# Revit family: Plumbing_Drainage_hansgrohe_56188XXX-RainDrain-Allround-Complete-set___555
name_source: partatom
category: Plumbing Fixtures
revit_build: Autodesk Revit 2018 (Build: 20170223_1515(x64)
units: mm (PartAtom-declared; Revit-internal decimal feet)

## family parameters
Cut with Voids When Loaded = Yes
Host = Face
OmniClass Number = 23.31.17.29
OmniClass Title = Shower Drains
Part Type = Normal
Room Calculation Point = No
Round Connector Dimension = Use Diameter
Shared = No

## types (2) — shared parameters
Always visible = Yes
BIMobject category = Drainage
Description = RainDrain Allround Complete set shower drain 900 for standard/flat installation
Design country = Germany
Edition number = 1
IFC Classification = Pipe Fitting
Manufacturer = Hansgrohe
Manufacturer country = Germany
Manufacturer name = hansgrohe
Masterformat 2014 Code = 22 13 19.13
Masterformat 2014 Description = Sanitary Drains
Material 1 = Hansgrohe - Plastic - Gray
Material 2 = Hansgrohe - Metal - 800 Stainless Steel Optic
Model = 56188XXX
OmniClass Code = 23-31 17 29
OmniClass Description = Shower Drains
Product Guid = f0647fe0-2ab4-4b4f-babe-186e32a229ca
Product SKU = 56188XXX
Product data url = https://bimobject.com
Product family = uBox universal
Product group = Concealed basic set shower drains
Product name = 56188XXX RainDrain Allround Complete set shower drain 900 for standard/flat installation
Product url = https://www.hansgrohe.com
QR code = https://bimobject.com
UNSPSC Code = 40141719
URL = https://www.hansgrohe.com
Uniclass 2015 Code = Pr_65_52_25
Uniclass 2015 Name = Drainage traps and accessories
Uniformat II Code = D2010
Uniformat II Description = Plumbing Fixtures
Weight Net (Kg) = 2.6
zero-valued in all types: Default Elevation

## per-type parameters (varying)
| type | Connector Description | Diameter | Installation | Installation - (Flat) | Installation - (Standard) |
| Installation Standard | Water Outlet 50 mm | 50  [stored 0.164042 ft] | 81 mm  [stored 0.265748 ft] | No | Yes |
| Installation Flat | Water Outlet 40 mm | 40 | 90 mm  [stored 0.295276 ft] | Yes | No |

note: [stored X ft] marks values corroborated as IEEE doubles in the binary element streams (Revit-internal decimal feet)

## geometry (parser evidence)
native form markers: Sweep x5
no freeform markers — native parametric forms only
